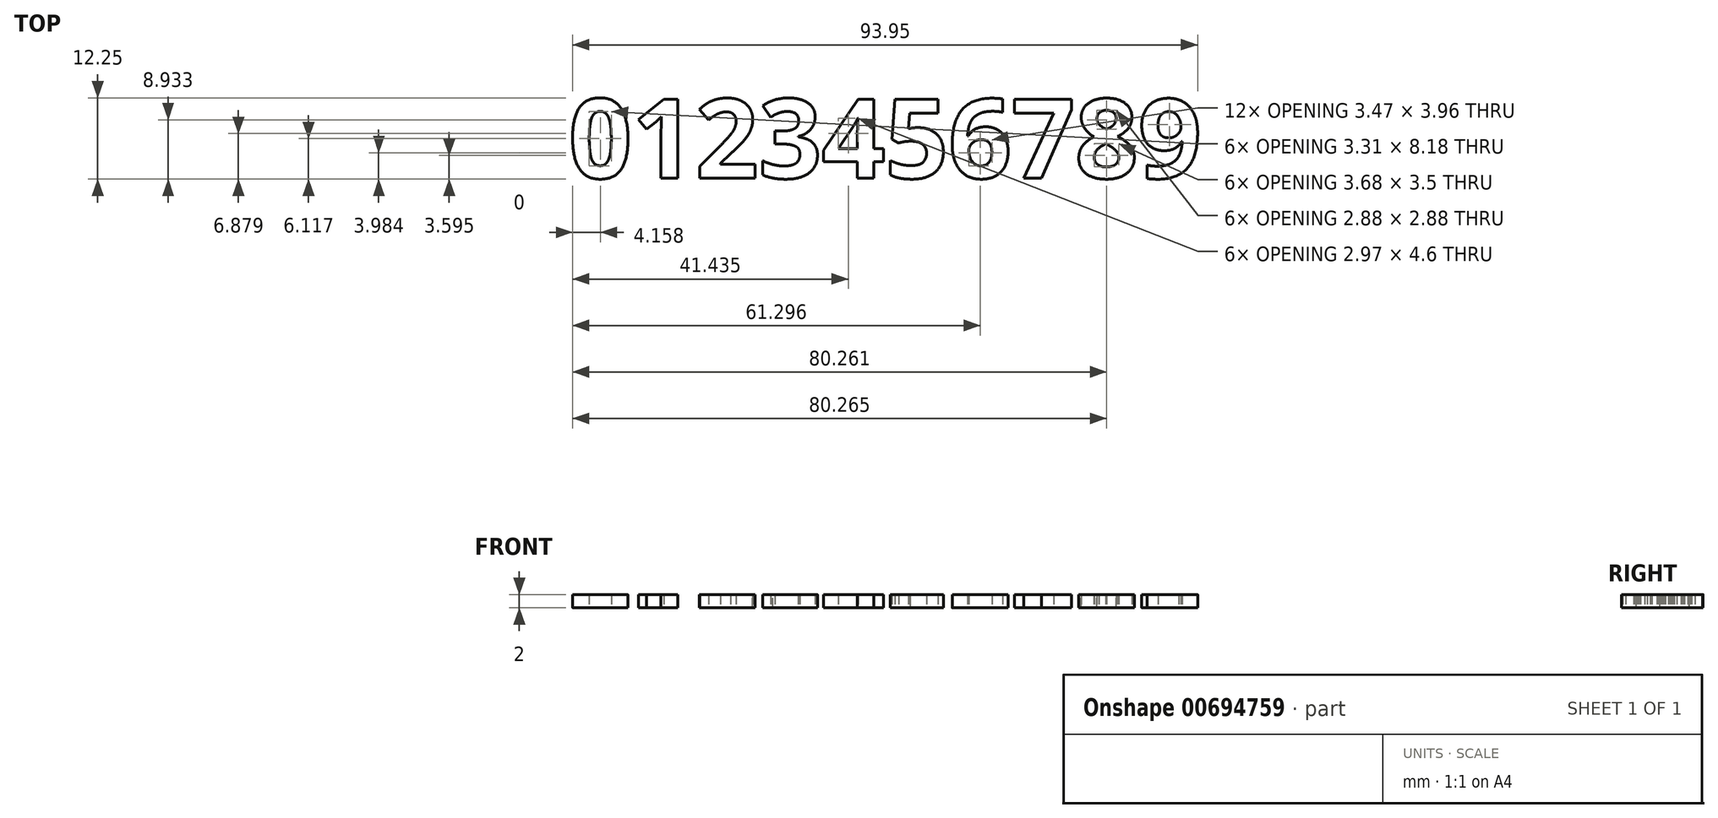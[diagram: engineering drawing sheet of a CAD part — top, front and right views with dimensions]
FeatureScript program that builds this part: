
annotation { "Feature Type Name" : "Feature", "Feature Type Description" : "" }
export const myFeature = defineFeature(function(context is Context, id is Id, definition is map)
    precondition{}
    {
        {
            var Q0;
            Q0=qCreatedBy(makeId("Top.planeOp"),FACE);
            var sketch = newSketch(context, id + "F0", { "sketchPlane" : qUnion([Q0])});
            skText(sketch, "E0", { "text": "0123456789", "fontName": "OpenSans-Bold.ttf"});
            const initialGuessF0  = {"E0": [0, 0, 1, 0, 0.012]};
            skSetInitialGuess(sketch, initialGuessF0);
            skSolve(sketch);
        }
        {
            var Q0;
            Q0 = qSketchRegion(id + "F0", true);
            extrude(context, id + "F1", {"entities" : qUnion([Q0]), "depth" : 2 * mm, "offsetDistance" : 25 * mm});
        }
    });
